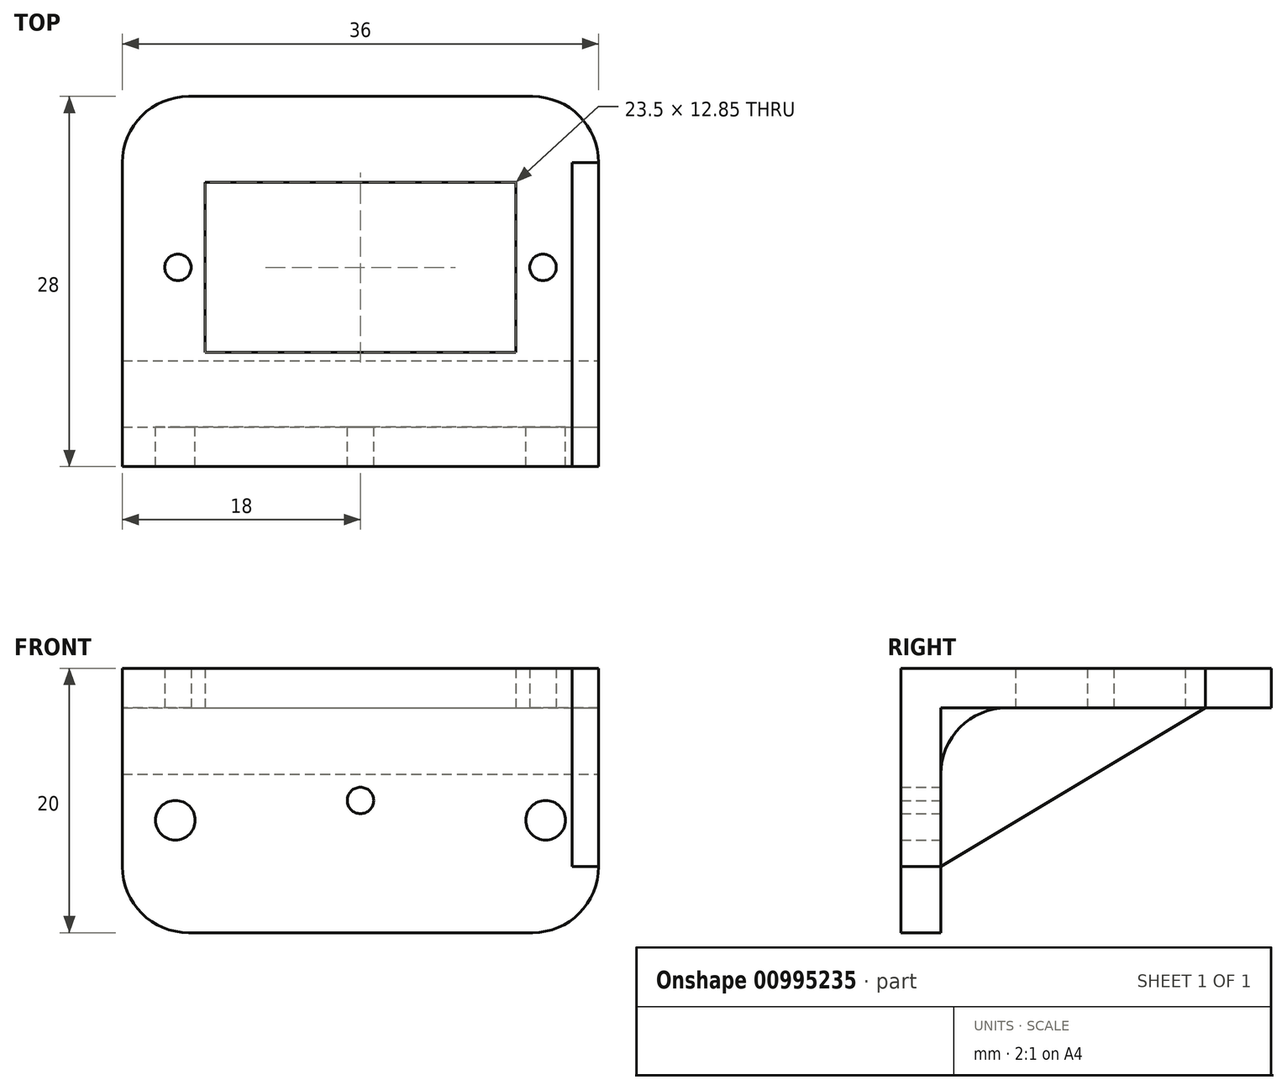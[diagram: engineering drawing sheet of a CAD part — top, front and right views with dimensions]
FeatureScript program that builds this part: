
annotation { "Feature Type Name" : "Feature", "Feature Type Description" : "" }
export const myFeature = defineFeature(function(context is Context, id is Id, definition is map)
    precondition{}
    {
        {
            var Q0;
            Q0=qCreatedBy(makeId("Front.planeOp"),FACE);
            var sketch = newSketch(context, id + "F0", { "sketchPlane" : qUnion([Q0])});
            skLineSegment(sketch, "E0.bottom", {"start": v(-5, 0) * mm, "end": v(-31, 0) * mm});
            skLineSegment(sketch, "E0.top", {"start": v(0, 17) * mm, "end": v(-36, 17) * mm});
            skLineSegment(sketch, "E0.left", {"start": v(0, 5) * mm, "end": v(0, 17) * mm});
            skLineSegment(sketch, "E0.right", {"start": v(-36, 5) * mm, "end": v(-36, 17) * mm});
            skPoint(sketch, "E1.visualSharp", {"position": v(-36, 0) * mm});
            skArc(sketch, "E1.filletArc", {"start": v(-36, 5) * mm, "mid": v(-34.54, 1.46) * mm, "end": v(-31, 0) * mm});
            skPoint(sketch, "E2.visualSharp", {"position": v(0, 0) * mm});
            skArc(sketch, "E2.filletArc", {"start": v(-5, 0) * mm, "mid": v(-1.46, 1.46) * mm, "end": v(0, 5) * mm});
            skLineSegment(sketch, "E3", {"start": v(4.06, 8.5) * mm, "end": v(-41.7, 8.5) * mm, "construction": true});
            skCircle(sketch, "E4", {"center": v(-4, 8.5) * mm, "radius": 1.5 * mm});
            skCircle(sketch, "E5", {"center": v(-32, 8.5) * mm, "radius": 1.5 * mm});
            skSolve(sketch);
        }
        {
            var Q0;
            Q0=makeQuery(id+"F0.imprint","IMPRINT",FACE,{"disambiguationData":[TD([[makeQuery(id+"F0.imprint","IMPRINT",EDGE,{"derivedFrom":sQuery(id+"F0.wireOp",EDGE,"E0.bottom")}),-1.0]])]});
            extrude(context, id + "F1", {"entities" : qUnion([Q0]), "depth" : 3 * mm, "offsetDistance" : 25 * mm});
        }
        {
            var Q0;
            Q0=makeQuery(id+"F1.opExtrude","SWEPT_FACE",FACE,{"disambiguationData":[OSD([sQuery(id+"F0.wireOp",EDGE,"E0.top")])]});
            var sketch = newSketch(context, id + "F2", { "sketchPlane" : qUnion([Q0])});
            skLineSegment(sketch, "E6.bottom", {"start": v(-36, -3) * mm, "end": v(0, -3) * mm});
            skLineSegment(sketch, "E6.top", {"start": v(-31, 25) * mm, "end": v(-5, 25) * mm});
            skLineSegment(sketch, "E6.left", {"start": v(-36, -3) * mm, "end": v(-36, 20) * mm});
            skLineSegment(sketch, "E6.right", {"start": v(0, -3) * mm, "end": v(0, 20) * mm});
            skLineSegment(sketch, "E7.bottom", {"start": v(-29.75, 18.5) * mm, "end": v(-6.25, 18.5) * mm});
            skLineSegment(sketch, "E7.top", {"start": v(-29.75, 5.65) * mm, "end": v(-6.25, 5.65) * mm});
            skLineSegment(sketch, "E7.left", {"start": v(-29.75, 18.5) * mm, "end": v(-29.75, 5.65) * mm});
            skLineSegment(sketch, "E7.right", {"start": v(-6.25, 18.5) * mm, "end": v(-6.25, 5.65) * mm});
            skPoint(sketch, "E8.visualSharp", {"position": v(-36, 25) * mm});
            skArc(sketch, "E8.filletArc", {"start": v(-31, 25) * mm, "mid": v(-34.54, 23.54) * mm, "end": v(-36, 20) * mm});
            skPoint(sketch, "E9.visualSharp", {"position": v(0, 25) * mm});
            skArc(sketch, "E9.filletArc", {"start": v(0, 20) * mm, "mid": v(-1.46, 23.54) * mm, "end": v(-5, 25) * mm});
            skCircle(sketch, "E10", {"center": v(-31.8, 12.07) * mm, "radius": 1 * mm});
            skCircle(sketch, "E11", {"center": v(-4.2, 12.08) * mm, "radius": 1 * mm});
            skSolve(sketch);
        }
        {
            var Q0;
            Q0=makeQuery(id+"F1.opExtrude","SWEPT_FACE",FACE,{"disambiguationData":[OSD([sQuery(id+"F0.wireOp",EDGE,"E0.bottom")])]});
            var Q1;
            Q1=makeQuery(id+"F2.imprint","IMPRINT",FACE,{"disambiguationData":[TD([[makeQuery(id+"F2.imprint","IMPRINT",EDGE,{"derivedFrom":sQuery(id+"F2.wireOp",EDGE,"E6.top")}),-1.0]])]});
            var Q2;
            {var subQ0=sQuery(id+"F2.wireOp",EDGE,"E6.bottom");Q2=makeQuery(id+"F2.imprint","IMPRINT",FACE,{"disambiguationData":[TD([[makeQuery(id+"F2.imprint","IMPRINT",EDGE,{"derivedFrom":subQ0}),-1.0]])]});}
            extrude(context, id + "F3", {"entities" : qUnion([Q0, Q1, Q2]), "operationType" : NewBodyOperationType.ADD, "oppositeDirection" : true, "depth" : 3 * mm, "offsetDistance" : 25 * mm});
        }
        {
            var Q0;
            Q0=makeQuery(id+"F3.boolean.opBoolean","MERGE",FACE,{"derivedFrom":[makeQuery(id+"F1.opExtrude","SWEPT_FACE",FACE,{"disambiguationData":[OSD([sQuery(id+"F0.wireOp",EDGE,"E0.left")])]}),makeQuery(id+"F3.opExtrude","SWEPT_FACE",FACE,{"disambiguationData":[OSD([sQuery(id+"F2.wireOp",EDGE,"E6.right")])]})]});
            var sketch = newSketch(context, id + "F4", { "sketchPlane" : qUnion([Q0])});
            skLineSegment(sketch, "E12", {"start": v(0, 12) * mm, "end": v(0, 5) * mm});
            skLineSegment(sketch, "E13", {"start": v(5, 17) * mm, "end": v(20, 17) * mm});
            skPoint(sketch, "E14.visualSharp", {"position": v(0, 17) * mm});
            skArc(sketch, "E14.filletArc", {"start": v(5, 17) * mm, "mid": v(1.46, 15.54) * mm, "end": v(0, 12) * mm});
            skSolve(sketch);
        }
        {
            var Q0;
            {var subQ0=sQuery(id+"F4.wireOp",EDGE,"E14.filletArc");Q0=makeQuery(id+"F4.imprint","IMPRINT",FACE,{"disambiguationData":[TD([[makeQuery(id+"F4.imprint","IMPRINT",EDGE,{"derivedFrom":subQ0}),-1.0]])]});}
            extrude(context, id + "F5", {"entities" : qUnion([Q0]), "oppositeDirection" : true, "depth" : 36 * mm, "offsetDistance" : 25 * mm});
        }
        {
            var Q0;
            Q0=makeQuery(id+"F1.opExtrude","CAP_FACE",FACE,{"disambiguationData":[OSD([sQuery(id+"F0.wireOp",EDGE,"E0.bottom"),sQuery(id+"F0.wireOp",EDGE,"E0.top"),sQuery(id+"F0.wireOp",EDGE,"E0.left"),sQuery(id+"F0.wireOp",EDGE,"E0.right"),sQuery(id+"F0.wireOp",EDGE,"EaoQwuJK-0JR3-WXCp-0gnX-JEyLQCxRJcx1"),sQuery(id+"F0.wireOp",EDGE,"zffFmAl6-EEWq-IfmN-EfRt-ywwZJMCpplNG"),sQuery(id+"F0.wireOp",EDGE,"7FfZNUnm-LjlD-sj8O-1Upn-dgazz33ehmct"),sQuery(id+"F0.wireOp",EDGE,"13s6ZXP5-RfvQ-Y6eU-VQyJ-W3zy3NvQVSSX"),sQuery(id+"F0.wireOp",EDGE,"E1.filletArc"),sQuery(id+"F0.wireOp",EDGE,"E2.filletArc")])],"isStart":true});
            var sketch = newSketch(context, id + "F6", { "sketchPlane" : qUnion([Q0])});
            skCircle(sketch, "E15", {"center": v(18, 10) * mm, "radius": 1 * mm});
            skSolve(sketch);
        }
        {
            var Q0;
            Q0=makeQuery(id+"F6.imprint","IMPRINT",FACE,{"disambiguationData":[TD([[makeQuery(id+"F6.imprint","IMPRINT",EDGE,{"derivedFrom":sQuery(id+"F6.wireOp",EDGE,"E15")}),1.0]])]});
            extrude(context, id + "F7", {"entities" : qUnion([Q0]), "operationType" : NewBodyOperationType.REMOVE, "endBound" : BoundingType.THROUGH_ALL, "oppositeDirection" : true, "depth" : 25 * mm, "offsetDistance" : 25 * mm});
        }
        {
            var Q0;
            Q0=makeQuery(id+"F3.boolean.opBoolean","MERGE",FACE,{"derivedFrom":[makeQuery(id+"F1.opExtrude","SWEPT_FACE",FACE,{"disambiguationData":[OSD([sQuery(id+"F0.wireOp",EDGE,"E0.left")])]}),makeQuery(id+"F3.opExtrude","SWEPT_FACE",FACE,{"disambiguationData":[OSD([sQuery(id+"F2.wireOp",EDGE,"E6.right")])]})]});
            var sketch = newSketch(context, id + "F8", { "sketchPlane" : qUnion([Q0])});
            skLineSegment(sketch, "E16", {"start": v(20, 17) * mm, "end": v(0, 5) * mm});
            skSolve(sketch);
        }
        {
            var Q0;
            Q0=makeQuery(id+"F8.imprint","IMPRINT",FACE,{"disambiguationData":[TD([[makeQuery(id+"F8.imprint","IMPRINT",EDGE,{"derivedFrom":sQuery(id+"F8.wireOp",EDGE,"E16")}),-1.0]])]});
            var Q1;
            {var subQ1=sQuery(id+"F0.wireOp",EDGE,"E0.left");Q1=makeQuery(id+"F8.imprint","IMPRINT",FACE,{"disambiguationData":[TD([[makeQuery(id+"F8.imprint","IMPRINT",EDGE,{"derivedFrom":makeQuery(id+"F1.opExtrude","CAP_EDGE",EDGE,{"disambiguationData":[OSD([subQ1])],"isStart":true})}),1.0]])]});}
            extrude(context, id + "F9", {"entities" : qUnion([Q0, Q1]), "oppositeDirection" : true, "depth" : 2 * mm, "offsetDistance" : 25 * mm});
        }
    });
